# Revit family: M3OA-27HFN8-Q
name_source: partatom
category: Attrezzatura meccanica
units: mm (PartAtom-declared; Revit-internal decimal feet)

## family parameters
Basato su piano di lavoro = No
Condiviso = No
Mantieni orientamento annotazione = No
Numero OmniClass = 23.75.00.00
Punto di calcolo locali = No
Quota connettore circolare = Usa diametro
Sempre verticale = Sì
Taglio con vuoti quando caricato = No
Tipo di parte = Normale
Titolo OmniClass = Climate Control (HVAC)

## types (1)
- T6
    Air Flow = 3500.00 m³/h
    Casing color = SB2098
    Compressor = 1
    Depth = 342 mm  [stored 1.12205 ft]
    Gas = R32
    Gas pipe = 9.52 mm
    Gas pipe Radius = 4.76 mm
    Height = 673 mm  [stored 2.20801 ft]
    Installation = Outdoor installation
    Liquid pipe = 6.35 mm  [stored 0.0208333 ft]
    Liquid pipe Radius = 3.175 mm  [stored 0.0104167 ft]
    Maximum Fuse Amps = 30 A
    Min cable selection (power wiring) = 2.5x3 mm2
    Minimum Circuit Amps = 18 A
    Modello = M3OA-27HFN8-Q
    Net Weight = 48.00 kg
    Power supply = 220-240V,1Ph, 50/60Hz
    Prospetto di default = 0 mm  [stored 0 ft]
    Width = 890 mm  [stored 2.91995 ft]
    clearance access behind = 300 mm  [stored 0.984252 ft]
    clearance access front = 2000 mm  [stored 6.56168 ft]
    clearance access left = 300 mm  [stored 0.984252 ft]
    clearance access right = 600 mm  [stored 1.9685 ft]

note: [stored X ft] marks values corroborated as IEEE doubles in the binary element streams (Revit-internal decimal feet)

## geometry (parser evidence)
native form markers: Blend x1, Sweep x32
no freeform markers — native parametric forms only
